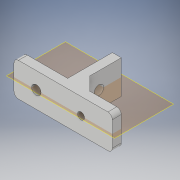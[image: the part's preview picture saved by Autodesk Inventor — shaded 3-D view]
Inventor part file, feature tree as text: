
AUTODESK INVENTOR PART (.ipt)
format: ipt  version: 2018 (Build 220112000, 112)  size: 151,552 bytes
history: native  units: in
note: dims shown in document units (in); Inventor stores cm internally (conversion verified against a paired STEP export)
features: extrude x5, sketch x5, projected_geometry x2, mirror x1, fillet x1
ambient origin geometry x8: Origin, YZ Plane, XZ Plane, XY Plane, X Axis, Y Axis, Z Axis, Center Point
bodies: Solid1 (feature_tree)
feature tree (14):
  extrude  "Extrusion1"  Depth=0.1575in
  extrude  "Extrusion2"  Depth=0.1575in
  extrude  "Extrusion3"  Depth=0.5906in TaperAngle=0.0deg
  extrude  "Extrusion4"  Depth=0.5906in TaperAngle=0.0deg
  extrude  "Extrusion5"  Depth=0.5906in TaperAngle=0.0deg
  mirror  "Mirror1"
  fillet  "Fillet1"  Radius=0.122in
  sketch  "Sketch1"  dims[d0=0.7874in d1=0.1575in]
  sketch  "Sketch2"  dims[d2=0.7874in d3=0.1575in]
  projected_geometry  "Projected Loop1"
  sketch  "Sketch3"  dims[d4=0.7874in d5=0.5906in d6=0.0in]
  projected_geometry  "Projected Loop2"
  sketch  "Sketch4"  dims[d7=0.1654in d8=0.5906in d9=0.0in]
  sketch  "Sketch5"  dims[d10=0.1654in d11=0.5906in d12=0.0in d13=0.122in d14=0.5512in d15=0.5906in d16=0.0in d17=0.2362in d18=0.2362in d19=0.1181in d20=0.0in d21=0.0787in]
